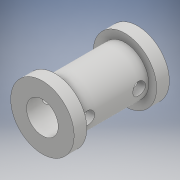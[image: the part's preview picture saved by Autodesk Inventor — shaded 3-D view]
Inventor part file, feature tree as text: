
AUTODESK INVENTOR PART (.ipt)
format: ipt  version: 2018 (Build 220112000, 112)  size: 163,840 bytes
history: native  units: mm
features: extrude x6, sketch x6, other x3
ambient origin geometry x8: Origin, YZ Plane, XZ Plane, XY Plane, X Axis, Y Axis, Z Axis, Center Point
bodies: Body1 (feature_tree)
feature tree (15):
  other  "Sólido1"
  extrude  "Extrusión1"  Depth=7.5mm
  extrude  "Extrusión2"  Depth=10.0mm
  extrude  "Extrusión3"  Depth=2.0mm TaperAngle=0.0deg
  extrude  "Extrusión4"  Depth=10.0mm TaperAngle=0.0deg
  extrude  "Extrusión5"  Depth=10.0mm TaperAngle=0.0deg
  extrude  "Extrusión6"  Depth=10.0mm
  other  "Edición directa1"
  sketch  "Boceto1"  dims[d1=5.0mm d2=7.5mm]
  sketch  "Boceto2"  dims[d3=10.0mm d4=0.0mm d5=10.0mm]
  sketch  "Boceto3"  dims[d6=2.0mm d7=0.0mm d8=2.0mm d9=0.0mm]
  sketch  "Boceto4"  dims[d10=5.0mm d11=10.0mm d12=0.0mm]
  sketch  "Boceto5"  dims[d13=5.0mm d14=10.0mm d15=0.0mm]
  sketch  "Boceto6"  dims[d16=1.5mm d17=1.5mm d18=2.0mm d19=10.0mm d20=0.0mm d21=0.0mm d22=0.0mm d23=5.0mm]
  other  "Desplazar1"
